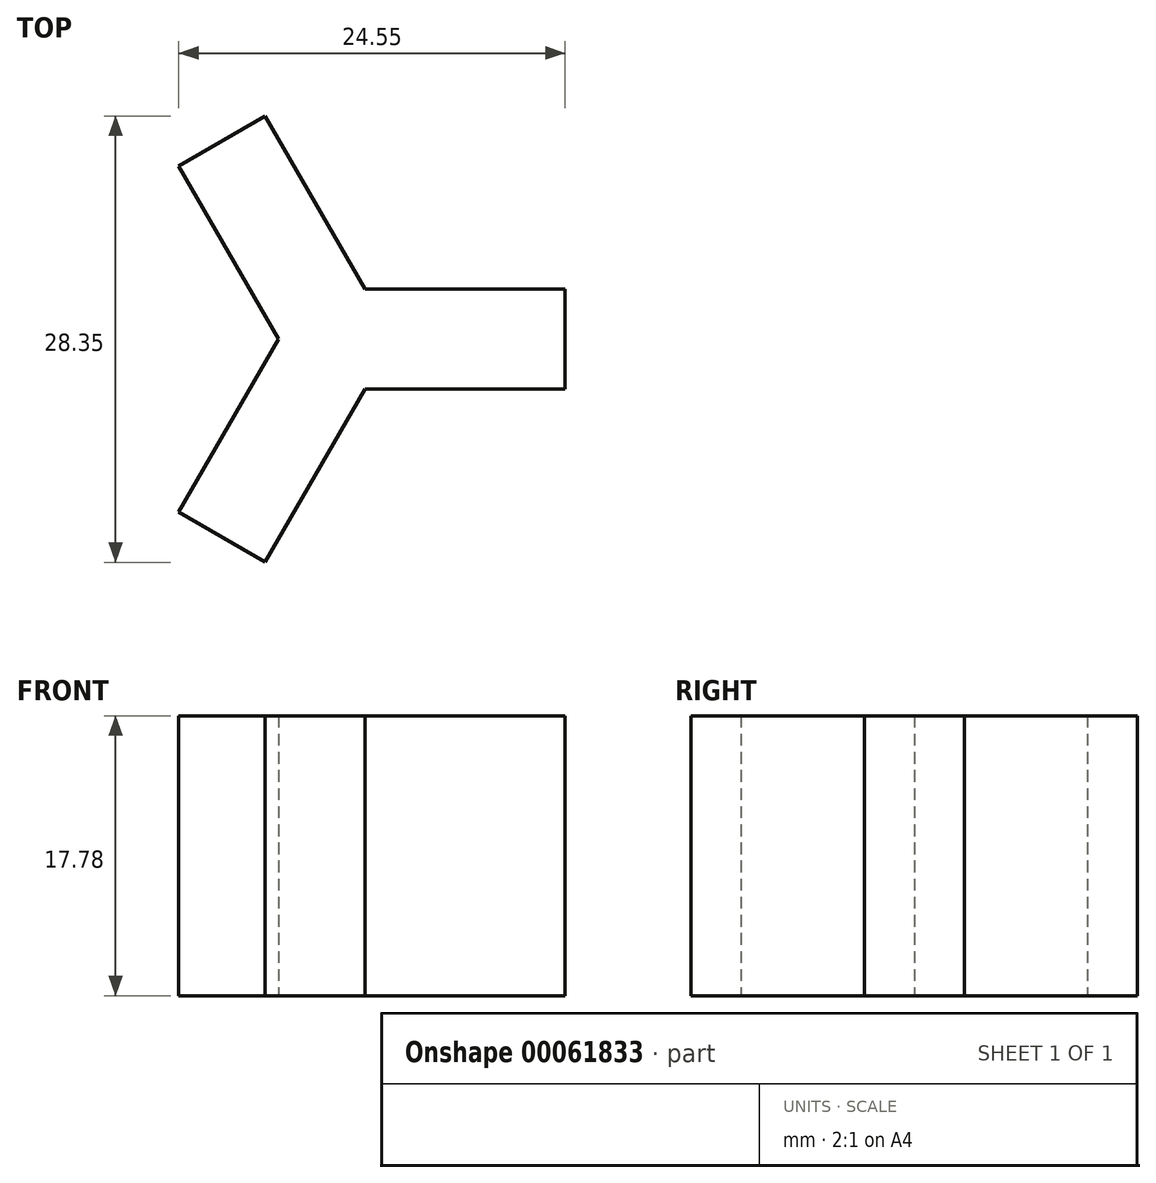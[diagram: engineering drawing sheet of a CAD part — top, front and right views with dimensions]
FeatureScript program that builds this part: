
annotation { "Feature Type Name" : "Feature", "Feature Type Description" : "" }
export const myFeature = defineFeature(function(context is Context, id is Id, definition is map)
    precondition{}
    {
        {
            var Q0;
            Q0=qCreatedBy(makeId("Top.planeOp"),FACE);
            var sketch = newSketch(context, id + "F0", { "sketchPlane" : qUnion([Q0])});
            skLineSegment(sketch, "E0.bottom", {"start": v(0, 6.35) * mm, "end": v(12.7, 6.35) * mm});
            skLineSegment(sketch, "E0.top", {"start": v(0, 0) * mm, "end": v(12.7, 0) * mm});
            skLineSegment(sketch, "E0.left", {"start": v(0, 6.35) * mm, "end": v(0, 0) * mm});
            skLineSegment(sketch, "E0.right", {"start": v(12.7, 6.35) * mm, "end": v(12.7, 0) * mm});
            skLineSegment(sketch, "E1", {"start": v(0, 0) * mm, "end": v(-6.35, -11) * mm});
            skLineSegment(sketch, "E2", {"start": v(-6.35, -11) * mm, "end": v(-11.85, -7.82) * mm});
            skLineSegment(sketch, "E3", {"start": v(-11.85, -7.82) * mm, "end": v(-5.5, 3.17) * mm});
            skLineSegment(sketch, "E4", {"start": v(-5.5, 3.17) * mm, "end": v(0, 0) * mm});
            skLineSegment(sketch, "E5", {"start": v(-5.5, 3.18) * mm, "end": v(-11.85, 14.17) * mm});
            skLineSegment(sketch, "E6", {"start": v(-11.85, 14.17) * mm, "end": v(-6.35, 17.35) * mm});
            skLineSegment(sketch, "E7", {"start": v(-6.35, 17.35) * mm, "end": v(0, 6.35) * mm});
            skLineSegment(sketch, "E8", {"start": v(0, 0) * mm, "end": v(-5.5, 3.17) * mm});
            skSolve(sketch);
        }
        {
            var Q0;
            Q0 = qSketchRegion(id + "F0", true);
            extrude(context, id + "F1", {"entities" : qUnion([Q0]), "depth" : 17.78 * mm});
        }
    });
